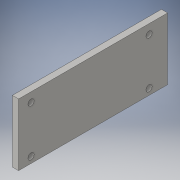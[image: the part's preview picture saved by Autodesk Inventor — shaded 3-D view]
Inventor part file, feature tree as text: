
AUTODESK INVENTOR PART (.ipt)
format: ipt  version: 2016 (Build 200138000, 138)  size: 100,352 bytes
history: native  units: in
note: dims shown in document units (in); Inventor stores cm internally (conversion verified against a paired STEP export)
features: sketch x2, extrude x1, hole x1
ambient origin geometry x8: Origin, YZ Plane, XZ Plane, XY Plane, X Axis, Y Axis, Z Axis, Center Point
bodies: Solid1 (feature_tree)
feature tree (4):
  extrude  "Extrusion1"  Depth=1.0in
  hole  "Hole1"  [1 undecoded]
  sketch  "Sketch1"  dims[d0=2.4in d1=1.0in]
  sketch  "Sketch2"  dims[d2=0.1in d3=0.0in d4=0.0in d5=0.0in d6=0.0in d7=0.0in d8=0.75in d9=0.1in d10=0.2in d11=1.9in d12=0.1in d13=0.75in d14=0.375in d15=0.25in d16=0.5635in d17=1.0in d18=0.8108in]
note: 1 required parameter value undecoded (feature->parameter linkage not recoverable at this tier; creation-order binding heuristic only, values carry confidence <= 0.55)
